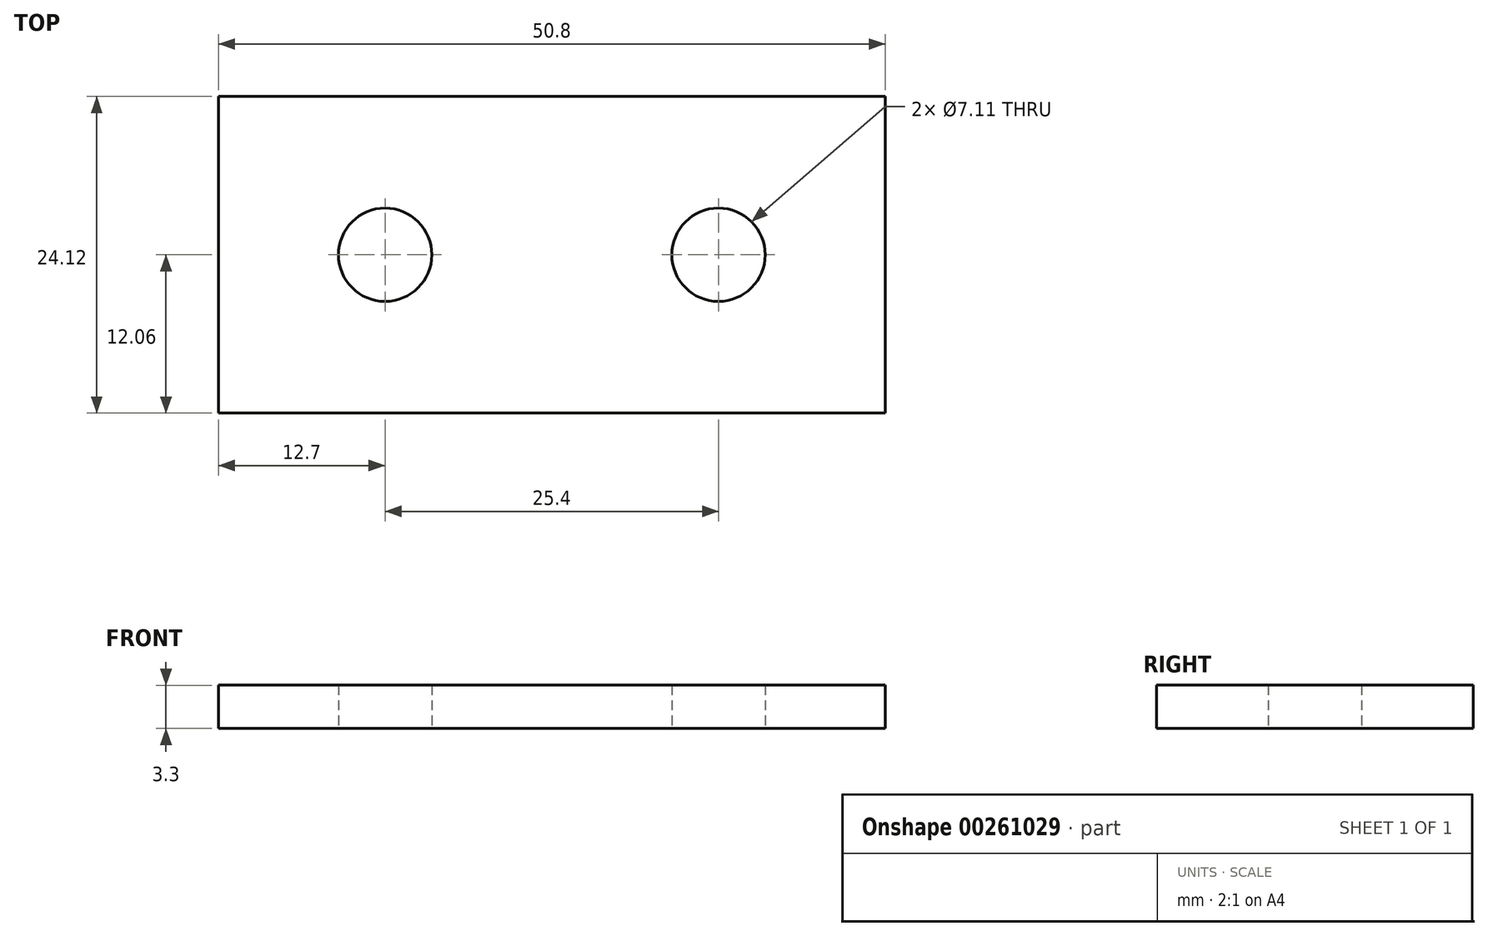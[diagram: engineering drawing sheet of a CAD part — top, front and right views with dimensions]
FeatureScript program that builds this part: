
annotation { "Feature Type Name" : "Feature", "Feature Type Description" : "" }
export const myFeature = defineFeature(function(context is Context, id is Id, definition is map)
    precondition{}
    {
        {
            var Q0;
            Q0=qCreatedBy(makeId("Top.planeOp"),FACE);
            var sketch = newSketch(context, id + "F0", { "sketchPlane" : qUnion([Q0])});
            skLineSegment(sketch, "E0.bottom", {"start": v(25.4, -12.07) * mm, "end": v(-25.4, -12.07) * mm});
            skLineSegment(sketch, "E0.top", {"start": v(25.4, 12.07) * mm, "end": v(-25.4, 12.07) * mm});
            skLineSegment(sketch, "E0.left", {"start": v(25.4, -12.07) * mm, "end": v(25.4, 12.07) * mm});
            skLineSegment(sketch, "E0.right", {"start": v(-25.4, -12.07) * mm, "end": v(-25.4, 12.07) * mm});
            skPoint(sketch, "E0.middle", {"position": v(0, 0) * mm});
            skPoint(sketch, "E1", {"position": v(-12.7, 0) * mm});
            skCircle(sketch, "E2", {"center": v(-12.7, 0) * mm, "radius": 3.56 * mm});
            skCircle(sketch, "E3.MirrorC", {"center": v(12.7, 0) * mm, "radius": 3.56 * mm});
            skSolve(sketch);
        }
        {
            var Q0;
            Q0=makeQuery(id+"F0.imprint","IMPRINT",FACE,{"disambiguationData":[TD([[makeQuery(id+"F0.imprint","IMPRINT",EDGE,{"derivedFrom":sQuery(id+"F0.wireOp",EDGE,"E0.bottom")}),-1.0]])]});
            extrude(context, id + "F1", {"entities" : qUnion([Q0]), "depth" : 3.3 * mm});
        }
    });
